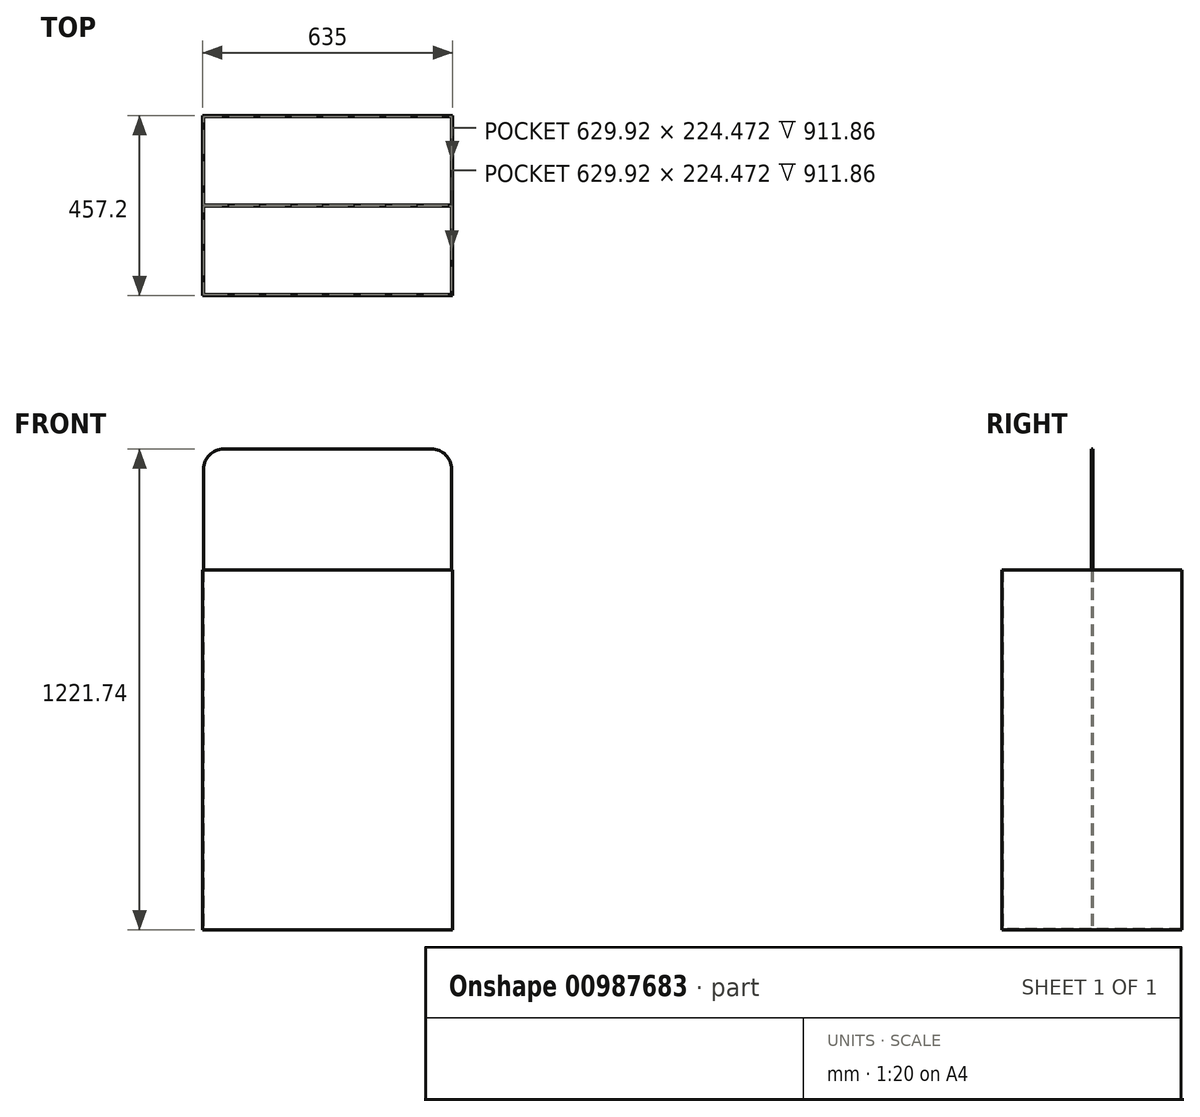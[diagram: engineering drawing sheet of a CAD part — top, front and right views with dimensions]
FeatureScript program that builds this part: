
annotation { "Feature Type Name" : "Feature", "Feature Type Description" : "" }
export const myFeature = defineFeature(function(context is Context, id is Id, definition is map)
    precondition{}
    {
        {
            var Q0;
            Q0=qCreatedBy(makeId("Top.planeOp"),FACE);
            var sketch = newSketch(context, id + "F0", { "sketchPlane" : qUnion([Q0])});
            skLineSegment(sketch, "E0", {"start": v(-317.5, 0) * mm, "end": v(317.5, 0) * mm, "construction": true});
            skLineSegment(sketch, "E1", {"start": v(0, 228.6) * mm, "end": v(0, -228.6) * mm, "construction": true});
            skLineSegment(sketch, "E2.bottom", {"start": v(-317.5, 228.6) * mm, "end": v(317.5, 228.6) * mm});
            skLineSegment(sketch, "E2.top", {"start": v(-317.5, -228.6) * mm, "end": v(317.5, -228.6) * mm});
            skLineSegment(sketch, "E2.left", {"start": v(-317.5, 228.6) * mm, "end": v(-317.5, -228.6) * mm});
            skLineSegment(sketch, "E2.right", {"start": v(317.5, 228.6) * mm, "end": v(317.5, -228.6) * mm});
            skSolve(sketch);
        }
        {
            var Q0;
            Q0 = qSketchRegion(id + "F0", true);
            extrude(context, id + "F1", {"entities" : qUnion([Q0]), "depth" : 914.4 * mm, "offsetDistance" : 25.4 * mm});
        }
        {
            var Q0;
            Q0=makeQuery(id+"F1.opExtrude","CAP_FACE",FACE,{"disambiguationData":[OSD([sQuery(id+"F0.wireOp",EDGE,"E2.bottom"),sQuery(id+"F0.wireOp",EDGE,"E2.top"),sQuery(id+"F0.wireOp",EDGE,"E2.left"),sQuery(id+"F0.wireOp",EDGE,"E2.right")])],"isStart":false});
            shell(context, id + "F2", {"entities" : qUnion([Q0]), "thickness" : 2.54 * mm});
        }
        {
            var Q0;
            Q0=makeQuery(id+"F2.opShell","OFFSET_FACE",FACE,{"disambiguationData":[OSD([sQuery(id+"F0.wireOp",EDGE,"E2.bottom"),sQuery(id+"F0.wireOp",EDGE,"E2.top"),sQuery(id+"F0.wireOp",EDGE,"E2.left"),sQuery(id+"F0.wireOp",EDGE,"E2.right")])]});
            var sketch = newSketch(context, id + "F3", { "sketchPlane" : qUnion([Q0])});
            skLineSegment(sketch, "E3", {"start": v(-314.96, 0) * mm, "end": v(314.96, 0) * mm, "construction": true});
            skLineSegment(sketch, "E4.bottom", {"start": v(-314.96, 1.59) * mm, "end": v(314.96, 1.59) * mm});
            skLineSegment(sketch, "E4.top", {"start": v(-314.96, -1.59) * mm, "end": v(314.96, -1.59) * mm});
            skLineSegment(sketch, "E4.left", {"start": v(-314.96, 1.59) * mm, "end": v(-314.96, -1.59) * mm});
            skLineSegment(sketch, "E4.right", {"start": v(314.96, 1.59) * mm, "end": v(314.96, -1.59) * mm});
            skSolve(sketch);
        }
        {
            var Q0;
            Q0 = qSketchRegion(id + "F3", true);
            extrude(context, id + "F4", {"entities" : qUnion([Q0]), "operationType" : NewBodyOperationType.ADD, "depth" : 1219.2 * mm, "offsetDistance" : 25.4 * mm});
        }
        {
            var Q0;
            Q0=makeQuery(id+"F4.opExtrude","CAP_EDGE",EDGE,{"disambiguationData":[OSD([sQuery(id+"F3.wireOp",EDGE,"E4.right")])],"isStart":false});
            var Q1;
            Q1=makeQuery(id+"F4.opExtrude","CAP_EDGE",EDGE,{"disambiguationData":[OSD([sQuery(id+"F3.wireOp",EDGE,"E4.left")])],"isStart":false});
            fillet(context, id + "F5", {"entities" : qUnion([Q0, Q1]), "tangentPropagation" : true, "radius" : 50.8 * mm, "defaultsChanged" : true, "vertexSettings" : [], "allowEdgeOverflow" : false});
        }
    });
